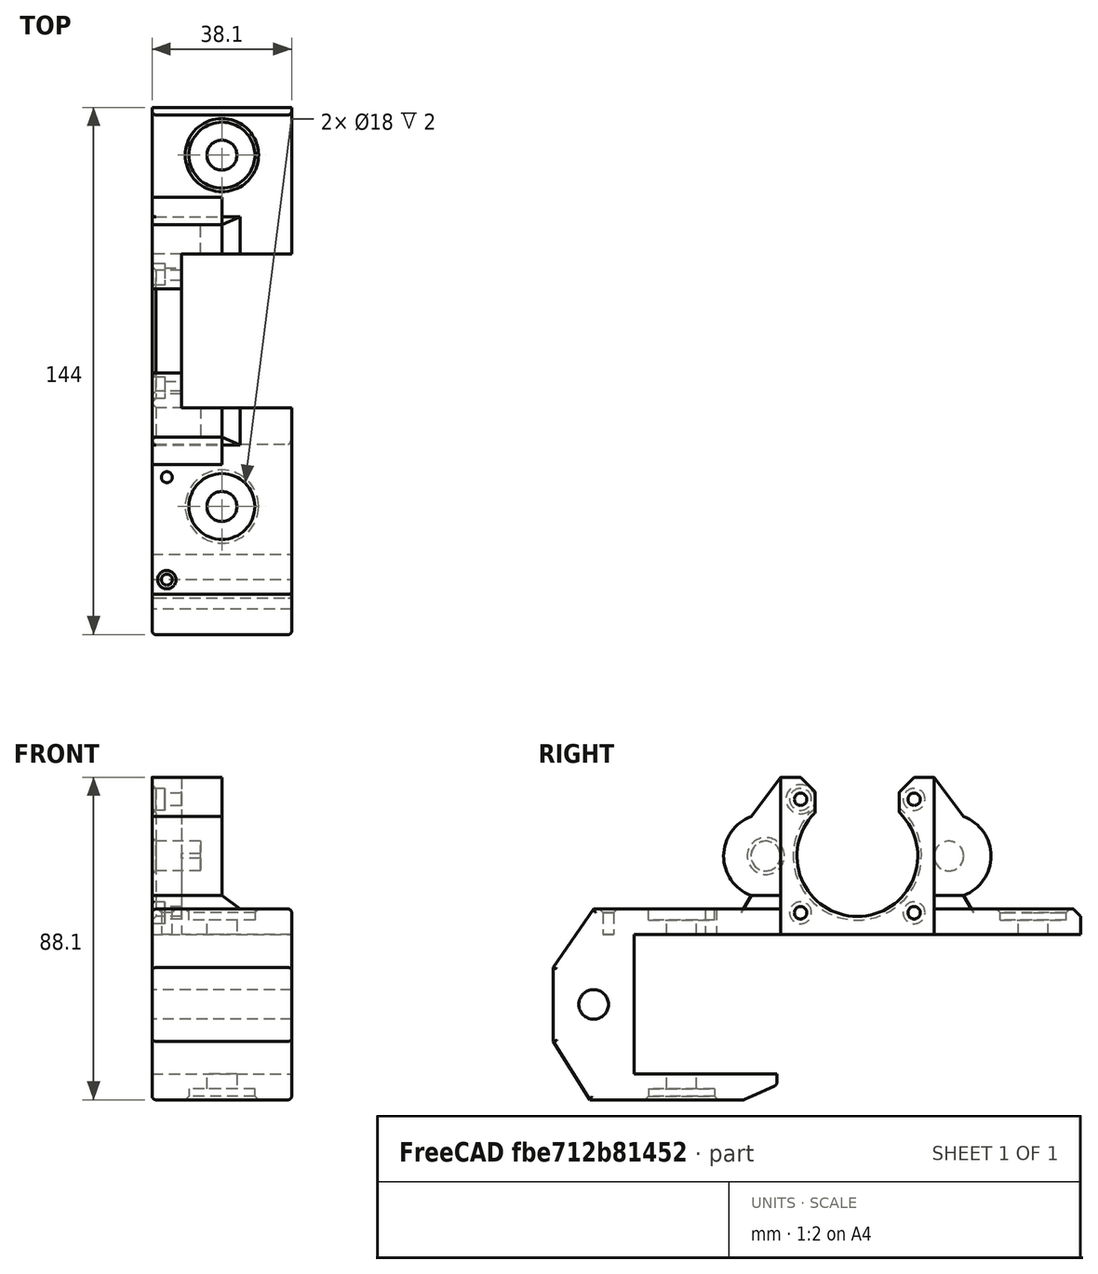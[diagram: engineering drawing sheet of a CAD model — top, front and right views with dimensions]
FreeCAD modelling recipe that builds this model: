
FCSTD DOCUMENT  (FreeCAD 0.19R21938 (Git))
Label: x-mount-left
License: All rights reserved
LicenseURL: http://en.wikipedia.org/wiki/All_rights_reserved
objects: Sketcher::SketchObject×10, PartDesign::Pocket×9, PartDesign::Fillet×3, PartDesign::Pad×1, Mesh::Feature×1, PartDesign::Chamfer×1, PartDesign::Body×1
note: 39 computed .brp shape members not serialized (recipe doc carries the construction recipe); baked Part::Feature solids carry a one-line shape summary decoded from their .brp

FEATURE [Sketcher::SketchObject] Sketch
  MapMode = 5
  Placement = pos=(0,0,0) rot=(0.57735,0.57735,0.57735;2.0944rad)
  Support = -> [YZ_Plane]
  sketch-geometry (30):
    g0: ArcOfCircle CenterX=-25 CenterY=21.5 CenterZ=0 NormalX=0 NormalY=0 NormalZ=1 AngleXU=0 Radius=11.5 StartAngle=1.92605 EndAngle=4.35714
    g1: ArcOfCircle CenterX=25 CenterY=21.5 CenterZ=0 NormalX=0 NormalY=0 NormalZ=1 AngleXU=0 Radius=11.5 StartAngle=5.06764 EndAngle=7.49873
    g2: LineSegment StartX=-31.1466 StartY=0 StartZ=0 EndX=-21 EndY=0 EndZ=0
    g3: LineSegment StartX=29 StartY=10.7181 StartZ=0 EndX=31.1466 EndY=7 EndZ=0
    g4: GeomPoint X=0 Y=21.5 Z=0
    g5: LineSegment StartX=-29 StartY=10.7181 StartZ=0 EndX=-31.1466 EndY=7 EndZ=0
    g6: LineSegment StartX=-61 StartY=0 StartZ=0 EndX=-31.1466 EndY=0 EndZ=0
    g7: LineSegment StartX=-72 StartY=7 StartZ=0 EndX=-31.1466 EndY=7 EndZ=0
    g8: LineSegment StartX=31.1466 StartY=7 StartZ=0 EndX=59 EndY=7 EndZ=0
    g9: LineSegment StartX=59 StartY=7 StartZ=0 EndX=61 EndY=5 EndZ=0
    g10: LineSegment StartX=61 StartY=5 StartZ=0 EndX=61 EndY=0 EndZ=0
    g11: LineSegment StartX=61 StartY=0 StartZ=0 EndX=-21 EndY=0 EndZ=0
    g12: LineSegment StartX=-21 StartY=43 StartZ=0 EndX=-15.5 EndY=43 EndZ=0
    g13: LineSegment StartX=-15.5 StartY=43 StartZ=0 EndX=-11.5 EndY=39 EndZ=0
    g14: LineSegment StartX=-11.5 StartY=39 StartZ=0 EndX=-11.5 EndY=33.3322 EndZ=0
    g15: LineSegment StartX=15.5 StartY=43 StartZ=0 EndX=11.5 EndY=39 EndZ=0
    g16: LineSegment StartX=11.5 StartY=39 StartZ=0 EndX=11.5 EndY=33.3322 EndZ=0
    g17: ArcOfCircle CenterX=0 CenterY=21.5 CenterZ=0 NormalX=0 NormalY=0 NormalZ=1 AngleXU=0 Radius=16.5 StartAngle=2.34196 EndAngle=7.08282
    g18: LineSegment StartX=15.5 StartY=43 StartZ=0 EndX=21 EndY=43 EndZ=0
    g19: LineSegment StartX=-21 StartY=43 StartZ=0 EndX=-29 EndY=32.2819 EndZ=0
    g20: LineSegment StartX=21 StartY=43 StartZ=0 EndX=29 EndY=32.2819 EndZ=0
    g21: GeomPoint X=0 Y=0 Z=0
    g22: LineSegment StartX=-61 StartY=0 StartZ=0 EndX=-61 EndY=-38.1 EndZ=0
    g23: LineSegment StartX=-61 StartY=-38.1 StartZ=0 EndX=-22 EndY=-38.1 EndZ=0
    g24: LineSegment StartX=-22 StartY=-38.1 StartZ=0 EndX=-22 EndY=-41.1 EndZ=0
    g25: LineSegment StartX=-72 StartY=7 StartZ=0 EndX=-83 EndY=-9 EndZ=0
    g26: LineSegment StartX=-83 StartY=-9 StartZ=0 EndX=-83 EndY=-29.1 EndZ=0
    g27: LineSegment StartX=-83 StartY=-29.1 StartZ=0 EndX=-73 EndY=-45.1 EndZ=0
    g28: LineSegment StartX=-73 StartY=-45.1 StartZ=0 EndX=-31 EndY=-45.1 EndZ=0
    g29: LineSegment StartX=-22 StartY=-41.1 StartZ=0 EndX=-31 EndY=-45.1 EndZ=0
  constraints (88):
    c: Diameter(g0) = 23
    c: Equal(g1,g0)
    c: DistanceX(g12,g2) = 0
    c: Horizontal(g2)
    c: Coincident(g1,g3)
    c: DistanceY(g4,g1) = 0
    c: Coincident(g5,g0)
    c: DistanceX(g12,g4) = 21
    c: Horizontal(g6)
    c: Horizontal(g7)
    c: DistanceY(g6,g7) = 7
    c: Coincident(g2,g6)
    c: Coincident(g5,g7)
    c: Horizontal(g8)
    c: Coincident(g9,g8)
    c: Coincident(g10,g9)
    c: Vertical(g10)
    c: Coincident(g11,g10)
    c: Horizontal(g11)
    c: DistanceX(g1,g1) = 0
    c: Coincident(g3,g8)
    c: DistanceY(g5,g3) = 0
    c: DistanceX(g8,g9) = 2
    c: DistanceX(g2,g5) = 0
    c: DistanceX(g1,g1) = 4
    c: Coincident(g14,g13)
    c: Vertical(g14)
    c: Coincident(g16,g15)
    c: Vertical(g16)
    c: Coincident(g17,g4)
    c: Diameter(g17) = 33
    c: DistanceY(g15,g13) = 0
    c: Coincident(g12,g13)
    c: Coincident(g18,g15)
    c: Tangent(g12,g18)
    c: Coincident(g17,g14)
    c: Coincident(g17,g16)
    c: DistanceX(g0,g0) = 0
    c: Coincident(g19,g0)
    c: Coincident(g20,g1)
    c: DistanceX(g12,g12) = 5.5
    c: Equal(g18,g12)
    c: DistanceX(g12,g13) = 4
    c: DistanceX(g15,g15) = 4
    c: Angle(g5,g7) = 2.0944
    c: Angle(g8,g3) = 2.0944
    c: Coincident(g2,g11)
    c: DistanceY(g13,g12) = 4
    c: PointOnObject(g21,g11)
    c: DistanceX(g4,g21) = 0
    c: DistanceY(g21,g4) = 21.5
    c: DistanceX(g0,g4) = 25
    c: Coincident(g12,g19)
    c: Coincident(g18,g20)
    c: DistanceY(g4,g12) = 21.5
    c: DistanceX(g0,g0) = 4
    c: DistanceX(g4,g1) = 25
    c: DistanceX(g12,g15) = 31
    c: DistanceX(g6,g21) = 61
    c: DistanceX(g21,g10) = 61
    c: Horizontal(g12)
    c: Coincident(g-1,g21)
    c: DistanceY(g4,g0) = 0
    c: Coincident(g22,g6)
    c: Vertical(g22)
    c: Coincident(g23,g22)
    c: Horizontal(g23)
    c: Coincident(g24,g23)
    c: Vertical(g24)
    c: Coincident(g25,g7)
    c: Coincident(g26,g25)
    c: Vertical(g26)
    c: Coincident(g27,g26)
    c: Coincident(g28,g27)
    c: Horizontal(g28)
    c: Coincident(g29,g24)
    c: Coincident(g29,g28)
    c: DistanceY(g22,g22) = 38.1
    c: DistanceX(g28,g28) = 42
    c: DistanceX(g23,g23) = 39
    c: DistanceY(g24,g24) = 3
    c: DistanceX(g28,g24) = 9
    c: DistanceX(g25,g6) = 22
    c: DistanceY(g25,g7) = 16
    c: DistanceY(g27,g26) = 16
    c: DistanceY(g28,g23) = 7
    c: DistanceX(g7,g6) = 11
    c: DistanceY(g10,g10) = 5
FEATURE [PartDesign::Pad] Pad
  AllowMultiFace = false
  Length = 38.1
  Length2 = 100
  Placement = pos=(0,0,0) rot=(0.57735,0.57735,0.57735;2.0944rad)
  Profile = -> Sketch
  Type = 0
FEATURE [Sketcher::SketchObject] Sketch001
  AttachmentOffset = pos=(0,0,7) rot=(0,0,1;0rad)
  MapMode = 5
  Placement = pos=(0,0,7) rot=(0,0,1;0rad)
  Support = -> [XY_Plane]
  sketch-geometry (2):
    g0: Circle CenterX=19.05 CenterY=48 CenterZ=0 NormalX=0 NormalY=0 NormalZ=1 AngleXU=0 Radius=9
    g1: Circle CenterX=19.05 CenterY=-48 CenterZ=0 NormalX=0 NormalY=0 NormalZ=1 AngleXU=0 Radius=9
  constraints (6):
    c: DistanceX(g-1,g0) = 19.05
    c: DistanceX(g0,g1) = 0
    c: Equal(g1,g0)
    c: Diameter(g0) = 18
    c: DistanceY(g-1,g0) = 48
    c: DistanceY(g1,g-1) = 48
FEATURE [Sketcher::SketchObject] Sketch002
  AttachmentOffset = pos=(0,0,50) rot=(0,0,1;0rad)
  MapMode = 5
  Placement = pos=(0,0,50) rot=(0,0,1;0rad)
  Support = -> [XY_Plane]
  sketch-geometry (6):
    g0: Circle CenterX=19.05 CenterY=48 CenterZ=0 NormalX=0 NormalY=0 NormalZ=1 AngleXU=0 Radius=4.1
    g1: Circle CenterX=19.05 CenterY=-48 CenterZ=0 NormalX=0 NormalY=0 NormalZ=1 AngleXU=0 Radius=4.1
    g2: LineSegment StartX=8 StartY=21 StartZ=0 EndX=58 EndY=21 EndZ=0
    g3: LineSegment StartX=58 StartY=21 StartZ=0 EndX=58 EndY=-21 EndZ=0
    g4: LineSegment StartX=58 StartY=-21 StartZ=0 EndX=8 EndY=-21 EndZ=0
    g5: LineSegment StartX=8 StartY=-21 StartZ=0 EndX=8 EndY=21 EndZ=0
  constraints (18):
    c: Equal(g1,g0)
    c: DistanceX(g1,g0) = 0
    c: DistanceX(g-1,g0) = 19.05
    c: Diameter(g0) = 8.2
    c: DistanceY(g-1,g0) = 48
    c: DistanceY(g1,g-1) = 48
    c: Coincident(g2,g3)
    c: Coincident(g3,g4)
    c: Coincident(g4,g5)
    c: Coincident(g5,g2)
    c: Horizontal(g2)
    c: Horizontal(g4)
    c: Vertical(g3)
    c: Vertical(g5)
    c: DistanceX(g-1,g2) = 8
    c: DistanceY(g5,g5) = 42
    c: DistanceY(g-1,g2) = 21
    c: DistanceX(g2,g2) = 50
FEATURE [PartDesign::Pocket] Pocket
  AllowMultiFace = false
  BaseFeature = -> Pad
  Length = 5
  Length2 = 100
  Placement = pos=(0,0,0) rot=(0.57735,0.57735,0.57735;2.0944rad)
  Profile = -> Sketch002
  Type = 1
FEATURE [PartDesign::Pocket] Pocket001
  AllowMultiFace = false
  BaseFeature = -> Pocket
  Length = 3
  Length2 = 100
  Placement = pos=(0,0,0) rot=(0.57735,0.57735,0.57735;2.0944rad)
  Profile = -> Sketch001
  Type = 0
FEATURE [Sketcher::SketchObject] Sketch003
  MapMode = 5
  Placement = pos=(0,0,0) rot=(0.57735,0.57735,0.57735;2.0944rad)
  Support = -> [YZ_Plane]
  sketch-geometry (2):
    g0: Circle CenterX=-25 CenterY=21.5 CenterZ=0 NormalX=0 NormalY=0 NormalZ=1 AngleXU=0 Radius=4.05
    g1: Circle CenterX=25 CenterY=21.5 CenterZ=0 NormalX=0 NormalY=0 NormalZ=1 AngleXU=0 Radius=4.05
  constraints (6):
    c: DistanceY(g1,g0) = 0
    c: Equal(g1,g0)
    c: Diameter(g0) = 8.1
    c: DistanceX(g0,g-1) = 25
    c: DistanceX(g-1,g1) = 25
    c: DistanceY(g-1,g0) = 21.5
FEATURE [PartDesign::Pocket] Pocket002
  AllowMultiFace = false
  BaseFeature = -> Pocket001
  Length = 13.2
  Length2 = 100
  Placement = pos=(0,0,0) rot=(0.57735,0.57735,0.57735;2.0944rad)
  Profile = -> Sketch003
  Reversed = true
  Type = 0
FEATURE [Sketcher::SketchObject] Sketch005
  MapMode = 5
  Placement = pos=(0,0,0) rot=(0.57735,0.57735,0.57735;2.0944rad)
  Support = -> [YZ_Plane]
  sketch-geometry (5):
    g0: Circle CenterX=-15.5 CenterY=37 CenterZ=0 NormalX=0 NormalY=0 NormalZ=1 AngleXU=0 Radius=3
    g1: Circle CenterX=15.5 CenterY=37 CenterZ=0 NormalX=0 NormalY=0 NormalZ=1 AngleXU=0 Radius=3
    g2: Circle CenterX=15.5 CenterY=6 CenterZ=0 NormalX=0 NormalY=0 NormalZ=1 AngleXU=0 Radius=3
    g3: Circle CenterX=-15.5 CenterY=6 CenterZ=0 NormalX=0 NormalY=0 NormalZ=1 AngleXU=0 Radius=3
    g4: GeomPoint X=0 Y=21.5 Z=0
  constraints (14):
    c: DistanceX(g3,g0) = 0
    c: DistanceX(g1,g2) = 0
    c: DistanceY(g0,g1) = 0
    c: DistanceY(g3,g2) = 0
    c: Diameter(g0) = 6
    c: Equal(g1,g0)
    c: Equal(g3,g0)
    c: Equal(g2,g0)
    c: DistanceX(g0,g4) = 15.5
    c: DistanceX(g0,g1) = 31
    c: DistanceY(g3,g0) = 31
    c: DistanceY(g4,g0) = 15.5
    c: PointOnObject(g4,g-2)
    c: DistanceY(g-1,g4) = 21.5
FEATURE [PartDesign::Pocket] Pocket003
  AllowMultiFace = false
  BaseFeature = -> Pocket002
  Length = 3.5
  Length2 = 100
  Placement = pos=(0,0,0) rot=(0.57735,0.57735,0.57735;2.0944rad)
  Profile = -> Sketch005
  Reversed = true
  Type = 0
FEATURE [Sketcher::SketchObject] Sketch006
  MapMode = 5
  Placement = pos=(0,0,0) rot=(0.57735,0.57735,0.57735;2.0944rad)
  Support = -> [YZ_Plane]
  sketch-geometry (5):
    g0: Circle CenterX=-15.5 CenterY=37 CenterZ=0 NormalX=0 NormalY=0 NormalZ=1 AngleXU=0 Radius=1.7
    g1: Circle CenterX=15.5 CenterY=37 CenterZ=0 NormalX=0 NormalY=0 NormalZ=1 AngleXU=0 Radius=1.7
    g2: Circle CenterX=15.5 CenterY=6 CenterZ=0 NormalX=0 NormalY=0 NormalZ=1 AngleXU=0 Radius=1.7
    g3: Circle CenterX=-15.5 CenterY=6 CenterZ=0 NormalX=0 NormalY=0 NormalZ=1 AngleXU=0 Radius=1.7
    g4: GeomPoint X=0 Y=21.5 Z=0
  constraints (14):
    c: DistanceX(g3,g0) = 0
    c: DistanceX(g1,g2) = 0
    c: DistanceY(g0,g1) = 0
    c: DistanceY(g3,g2) = 0
    c: Diameter(g0) = 3.4
    c: Equal(g1,g0)
    c: Equal(g3,g0)
    c: Equal(g2,g0)
    c: DistanceX(g0,g4) = 15.5
    c: DistanceX(g0,g1) = 31
    c: DistanceY(g3,g0) = 31
    c: DistanceY(g4,g0) = 15.5
    c: PointOnObject(g4,g-2)
    c: DistanceY(g-1,g4) = 21.5
FEATURE [PartDesign::Pocket] Pocket004
  AllowMultiFace = false
  BaseFeature = -> Pocket003
  Length = 5
  Length2 = 100
  Placement = pos=(0,0,0) rot=(0.57735,0.57735,0.57735;2.0944rad)
  Profile = -> Sketch006
  Reversed = true
  Type = 1
FEATURE [Sketcher::SketchObject] Sketch017
  AttachmentOffset = pos=(0,0,37) rot=(0,0,1;0rad)
  MapMode = 5
  Placement = pos=(0,-37,-8.2e-15) rot=(1,0,0;1.5708rad)
  Support = -> [XZ_Plane]
  sketch-geometry (6):
    g0: LineSegment StartX=19.05 StartY=10.75 StartZ=0 EndX=24.05 EndY=7 EndZ=0
    g1: LineSegment StartX=24.05 StartY=7 StartZ=0 EndX=38.1 EndY=7 EndZ=0
    g2: LineSegment StartX=38.1 StartY=7 StartZ=0 EndX=38.1 EndY=10.75 EndZ=0
    g3: LineSegment StartX=19.05 StartY=10.75 StartZ=0 EndX=19.05 EndY=43.75 EndZ=0
    g4: LineSegment StartX=19.05 StartY=43.75 StartZ=0 EndX=38.1 EndY=43.75 EndZ=0
    g5: LineSegment StartX=38.1 StartY=43.75 StartZ=0 EndX=38.1 EndY=10.75 EndZ=0
  constraints (18):
    c: Coincident(g1,g0)
    c: Horizontal(g1)
    c: Coincident(g2,g1)
    c: Vertical(g2)
    c: DistanceX(g0,g2) = 19.05
    c: DistanceY(g2,g2) = 3.75
    c: DistanceX(g0,g0) = 5
    c: DistanceX(g-1,g0) = 19.05
    c: DistanceY(g-1,g0) = 7
    c: Vertical(g3)
    c: Horizontal(g4)
    c: Coincident(g5,g4)
    c: Vertical(g5)
    c: Coincident(g3,g4)
    c: Coincident(g2,g5)
    c: Coincident(g0,g3)
    c: DistanceY(g5,g5) = 33
    c: DistanceY(g0,g0) = 3.75
FEATURE [PartDesign::Pocket] Pocket005
  AllowMultiFace = false
  BaseFeature = -> Pocket004
  Length = 5
  Length2 = 100
  Placement = pos=(0,0,0) rot=(0.57735,0.57735,0.57735;2.0944rad)
  Profile = -> Sketch017
  Type = 1
FEATURE [Sketcher::SketchObject] Sketch019
  MapMode = 5
  Support = -> [XY_Plane]
  sketch-geometry (2):
    g0: Circle CenterX=4 CenterY=-40 CenterZ=0 NormalX=0 NormalY=0 NormalZ=1 AngleXU=0 Radius=1.5
    g1: Circle CenterX=4 CenterY=-68 CenterZ=0 NormalX=0 NormalY=0 NormalZ=1 AngleXU=0 Radius=1.5
  constraints (6):
    c: DistanceX(g1,g0) = 0
    c: Equal(g1,g0)
    c: DistanceX(g-1,g0) = 4
    c: DistanceY(g0,g-1) = 40
    c: DistanceY(g1,g0) = 28
    c: Diameter(g1) = 3
FEATURE [PartDesign::Pocket] Pocket006
  AllowMultiFace = false
  BaseFeature = -> Pocket005
  Length = 5
  Length2 = 100
  Placement = pos=(0,0,0) rot=(0.57735,0.57735,0.57735;2.0944rad)
  Profile = -> Sketch019
  Reversed = true
  Type = 1
FEATURE [Mesh::Feature] x_mount_right  label="x-mount-right001"
  Placement = pos=(702,-8.6e-14,0) rot=(0,0,1;3.14159rad)
FEATURE [Sketcher::SketchObject] Sketch020
  AttachmentOffset = pos=(0,0,-45.1) rot=(0,0,1;0rad)
  MapMode = 5
  Placement = pos=(0,0,-45.1) rot=(0,0,1;0rad)
  Support = -> [XY_Plane]
  sketch-geometry (1):
    g0: Circle CenterX=19.05 CenterY=-48 CenterZ=0 NormalX=0 NormalY=0 NormalZ=1 AngleXU=0 Radius=9
  constraints (3):
    c: DistanceX(g-1,g0) = 19.05
    c: DistanceY(g0,g-1) = 48
    c: Diameter(g0) = 18
FEATURE [PartDesign::Pocket] Pocket007
  AllowMultiFace = false
  BaseFeature = -> Pocket006
  Length = 3
  Length2 = 100
  Placement = pos=(0,0,0) rot=(0.57735,0.57735,0.57735;2.0944rad)
  Profile = -> Sketch020
  Reversed = true
  Type = 0
FEATURE [PartDesign::Chamfer] Chamfer
  Angle = 45
  Base = -> Pocket007 [Edge102,Edge165,Edge166,Edge12,Edge66,Edge37,Edge38,Edge84]
  BaseFeature = -> Pocket007
  ChamferType = 0
  FlipDirection = false
  Placement = pos=(0,0,0) rot=(0.57735,0.57735,0.57735;2.0944rad)
  Size = 1
  Size2 = 1
  SupportTransform = false
FEATURE [PartDesign::Fillet] Fillet
  Base = -> Chamfer [Edge31,Edge32,Edge29,Edge30]
  BaseFeature = -> Chamfer
  Placement = pos=(0,0,0) rot=(0.57735,0.57735,0.57735;2.0944rad)
  Radius = 0.5
  SupportTransform = false
FEATURE [PartDesign::Fillet] Fillet001
  Base = -> Fillet [Edge17,Edge14,Edge16,Edge18,Edge20,Edge22,Edge168,Edge172,Edge160,Edge159,Edge70,Edge78,Edge84,Edge89,Edge93,Edge100,Edge86]
  BaseFeature = -> Fillet
  Placement = pos=(0,0,0) rot=(0.57735,0.57735,0.57735;2.0944rad)
  Radius = 1
  SupportTransform = false
FEATURE [PartDesign::Fillet] Fillet002
  Base = -> Fillet001 [Edge67,Edge73,Edge76,Edge82,Edge102,Edge98,Edge90,Edge91]
  BaseFeature = -> Fillet001
  Placement = pos=(0,0,0) rot=(0.57735,0.57735,0.57735;2.0944rad)
  Radius = 0.5
  SupportTransform = false
FEATURE [Sketcher::SketchObject] Sketch021
  MapMode = 5
  Placement = pos=(0,0,0) rot=(0.57735,0.57735,0.57735;2.0944rad)
  Support = -> [YZ_Plane]
  sketch-geometry (1):
    g0: Circle CenterX=-72 CenterY=-19.05 CenterZ=0 NormalX=0 NormalY=0 NormalZ=1 AngleXU=0 Radius=4.05
  constraints (3):
    c: DistanceX(g0,g-1) = 72
    c: Diameter(g0) = 8.1
    c: DistanceY(g0,g-1) = 19.05
FEATURE [PartDesign::Pocket] Pocket008
  AllowMultiFace = false
  BaseFeature = -> Fillet002
  Length = 5
  Length2 = 100
  Placement = pos=(0,0,0) rot=(0.57735,0.57735,0.57735;2.0944rad)
  Profile = -> Sketch021
  Reversed = true
  Type = 1
FEATURE [PartDesign::Body] Body  label="x-mount-left"
  Group = -> [Sketch,Pad,Sketch002,Pocket,Sketch001,Pocket001,Sketch003,Pocket002,Sketch005,Pocket003,Sketch006,Pocket004,Sketch017,Pocket005,Sketch019,Pocket006,Sketch020,Pocket007,Chamfer,Fillet,Fillet001,Fillet002,Sketch021,Pocket008]
  Origin = -> Origin
  Placement = pos=(332,0,0) rot=(0,0,1;0rad)
  Tip = -> Pocket008
